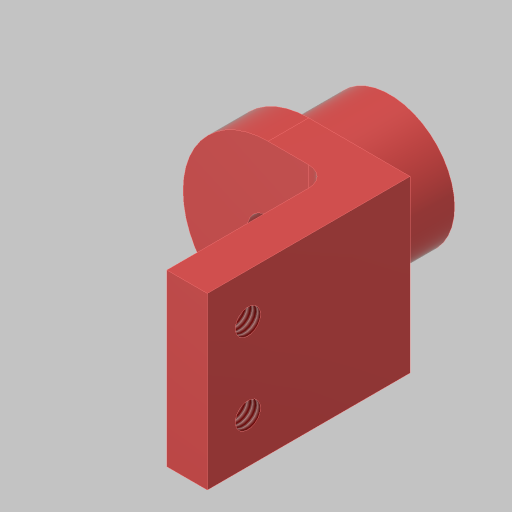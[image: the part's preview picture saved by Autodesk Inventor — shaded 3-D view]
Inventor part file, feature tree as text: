
AUTODESK INVENTOR PART (.ipt)
format: ipt  version: 2023.5 (Build 275446000, 446)  size: 149,504 bytes
history: native  units: in
note: dims shown in document units (in); Inventor stores cm internally (conversion verified against a paired STEP export)
features: sketch x5, extrude x3, hole x2, fillet x1, projected_geometry x1
ambient origin geometry x8: Origin, YZ Plane, XZ Plane, XY Plane, X Axis, Y Axis, Z Axis, Center Point
bodies: Solid1 (feature_tree)
feature tree (12):
  extrude  "Extrusion1"  Depth=0.5in TaperAngle=0.0deg
  extrude  "Extrusion2"  Depth=0.25in TaperAngle=0.0deg
  hole  "Hole2"  [1 undecoded]
  extrude  "Extrusion3"  Depth=0.25in
  fillet  "Fillet1"  Radius=1.0in
  hole  "Hole3"  [1 undecoded]
  sketch  "Sketch1"  dims[d0=0.8in d1=0.5in d2=0.0in]
  sketch  "Sketch2"  dims[d3=0.125in d4=0.25in d5=0.0in]
  sketch  "Sketch4"  dims[d6=0.688in d14=0.625in]
  sketch  "Sketch5"  dims[d15=0.257in d16=0.75in d17=0.375in d18=0.25in d19=0.5635in d20=1.0in d21=0.8108in d22=0.25in d23=1.0in d24=0.0in]
  sketch  "Sketch6"  dims[d25=0.125in d26=0.5in d27=0.156in d28=0.38in d29=0.385in d30=0.25in d31=0.5635in d32=1.0in d33=0.8108in d34=0.25in]
  projected_geometry  "Project Cut Edges1"
note: 2 required parameter values undecoded (feature->parameter linkage not recoverable at this tier; creation-order binding heuristic only, values carry confidence <= 0.55)
